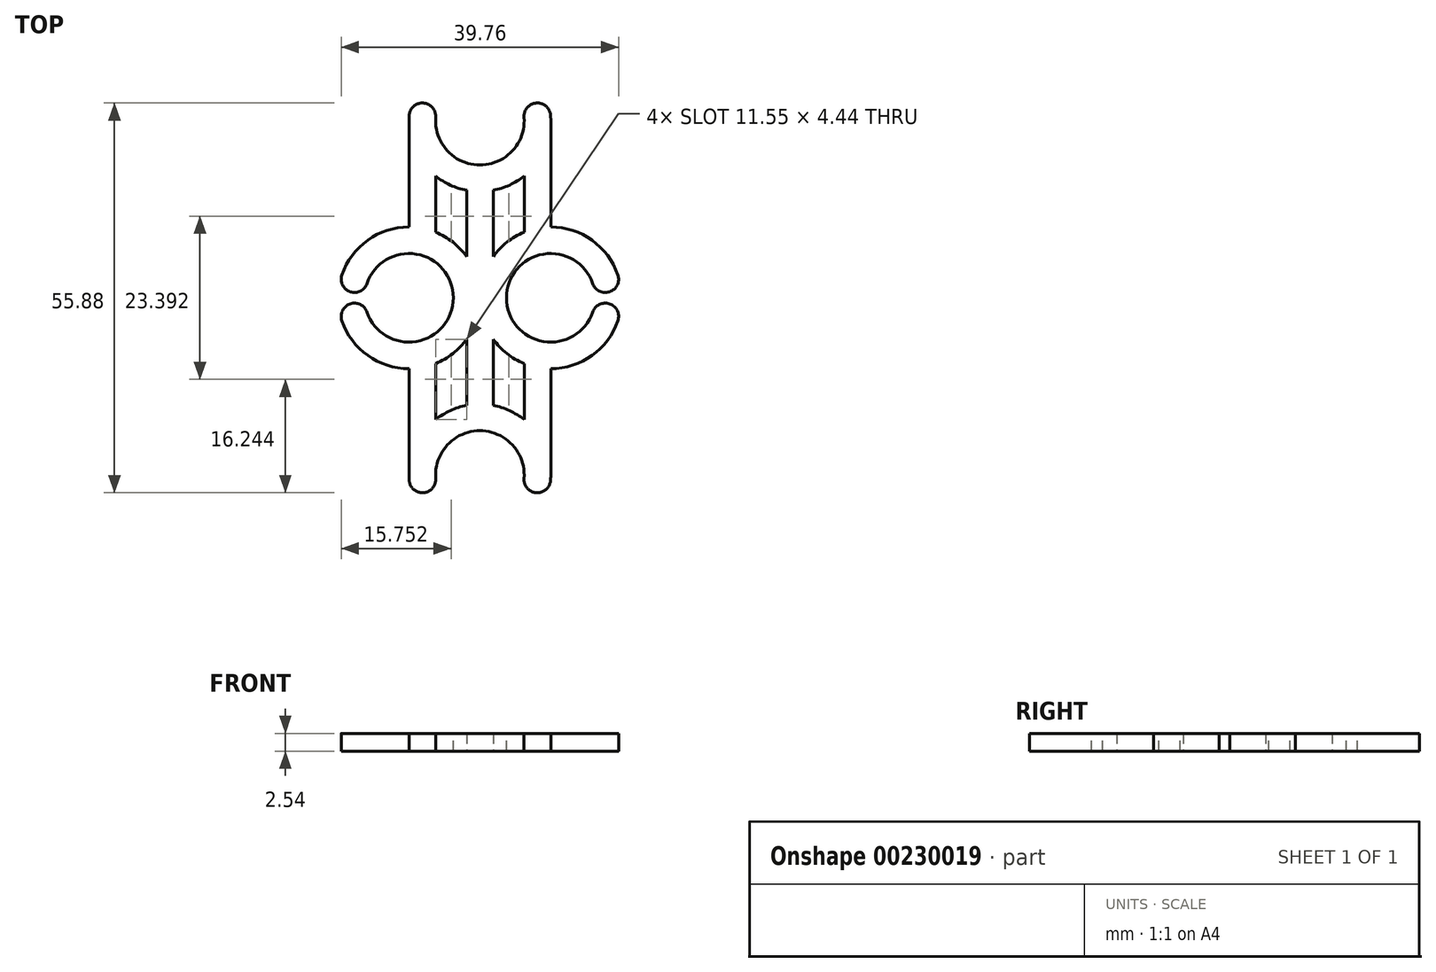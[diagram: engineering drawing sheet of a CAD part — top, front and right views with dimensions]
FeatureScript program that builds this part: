
annotation { "Feature Type Name" : "Feature", "Feature Type Description" : "" }
export const myFeature = defineFeature(function(context is Context, id is Id, definition is map)
    precondition{}
    {
        {
            var Q0;
            Q0=qCreatedBy(makeId("Top.planeOp"),FACE);
            var sketch = newSketch(context, id + "F0", { "sketchPlane" : qUnion([Q0])});
            skLineSegment(sketch, "E0", {"start": v(0, -25.4) * mm, "end": v(0, 25.4) * mm, "construction": true});
            skArc(sketch, "E1", {"start": v(-9.84, 27.94) * mm, "mid": v(0, 15.24) * mm, "end": v(9.84, 27.94) * mm});
            skArc(sketch, "E2", {"start": v(9.84, -27.94) * mm, "mid": v(0, -15.24) * mm, "end": v(-9.84, -27.94) * mm});
            skLineSegment(sketch, "E3.bottom", {"start": v(-1.9, 25.4) * mm, "end": v(1.9, 25.4) * mm});
            skLineSegment(sketch, "E3.top", {"start": v(-1.9, -25.4) * mm, "end": v(1.9, -25.4) * mm});
            skLineSegment(sketch, "E3.left", {"start": v(-1.9, 25.4) * mm, "end": v(-1.9, -25.4) * mm});
            skLineSegment(sketch, "E3.right", {"start": v(1.9, 25.4) * mm, "end": v(1.9, -25.4) * mm});
            skLineSegment(sketch, "E4", {"start": v(-9.84, 27.94) * mm, "end": v(9.84, 27.94) * mm});
            skLineSegment(sketch, "E5", {"start": v(-9.84, -27.94) * mm, "end": v(9.84, -27.94) * mm});
            skLineSegment(sketch, "E6", {"start": v(-10.16, 0) * mm, "end": v(10.16, 0) * mm, "construction": true});
            skPoint(sketch, "E7", {"position": v(0, 0) * mm});
            skCircle(sketch, "E8", {"center": v(-10.16, 0) * mm, "radius": 10.16 * mm});
            skCircle(sketch, "E9", {"center": v(10.16, 0) * mm, "radius": 10.16 * mm});
            skSolve(sketch);
        }
        {
            var Q0;
            Q0 = qSketchRegion(id + "F0", true);
            extrude(context, id + "F1", {"entities" : qUnion([Q0]), "depth" : 2.54 * mm});
        }
        {
            var Q0;
            Q0=makeQuery(id+"F1.opExtrude","CAP_FACE",FACE,{"disambiguationData":[OSD([sQuery(id+"F0.wireOp",EDGE,"Vd3e2Aaa-RSyU-HRI3-QYuA-ZNUXVVFevwxr"),sQuery(id+"F0.wireOp",EDGE,"BYLcNjdj-XaZf-7qvr-jPH4-58Jk393fSOor"),sQuery(id+"F0.wireOp",EDGE,"E1"),sQuery(id+"F0.wireOp",EDGE,"E2"),sQuery(id+"F0.wireOp",EDGE,"E3.left"),sQuery(id+"F0.wireOp",EDGE,"E3.right"),sQuery(id+"F0.wireOp",EDGE,"E4"),sQuery(id+"F0.wireOp",EDGE,"E5")])],"isStart":false});
            var sketch = newSketch(context, id + "F2", { "sketchPlane" : qUnion([Q0])});
            skCircle(sketch, "E10", {"center": v(0, 25.4) * mm, "radius": 6.35 * mm});
            skCircle(sketch, "E11", {"center": v(10.16, 0) * mm, "radius": 6.35 * mm});
            skCircle(sketch, "E12", {"center": v(-10.16, 0) * mm, "radius": 6.35 * mm});
            skCircle(sketch, "E13", {"center": v(0, -25.4) * mm, "radius": 6.35 * mm});
            skSolve(sketch);
        }
        {
            var Q0;
            Q0 = qSketchRegion(id + "F2", true);
            extrude(context, id + "F3", {"entities" : qUnion([Q0]), "operationType" : NewBodyOperationType.REMOVE, "oppositeDirection" : true, "depth" : 25.4 * mm});
        }
        {
            var Q0;
            Q0=makeQuery(id+"F1.opExtrude","CAP_FACE",FACE,{"disambiguationData":[OSD([sQuery(id+"F0.wireOp",EDGE,"E1"),sQuery(id+"F0.wireOp",EDGE,"E2"),sQuery(id+"F0.wireOp",EDGE,"E3.left"),sQuery(id+"F0.wireOp",EDGE,"E3.right"),sQuery(id+"F0.wireOp",EDGE,"E4"),sQuery(id+"F0.wireOp",EDGE,"E5"),sQuery(id+"F0.wireOp",EDGE,"E8"),sQuery(id+"F0.wireOp",EDGE,"E9")])],"isStart":false});
            var sketch = newSketch(context, id + "F4", { "sketchPlane" : qUnion([Q0])});
            skLineSegment(sketch, "E14", {"start": v(10.16, -25.4) * mm, "end": v(10.16, -10.16) * mm});
            skLineSegment(sketch, "E15", {"start": v(6.35, -17.47) * mm, "end": v(6.35, -9.42) * mm});
            skArc(sketch, "E16", {"start": v(10.16, -25.4) * mm, "mid": v(9.16, -21) * mm, "end": v(6.35, -17.47) * mm});
            skArc(sketch, "E17", {"start": v(6.35, -9.42) * mm, "mid": v(8.22, -9.97) * mm, "end": v(10.16, -10.16) * mm});
            skLineSegment(sketch, "E18.MirrorCS", {"start": v(-6.35, -17.47) * mm, "end": v(-6.35, -9.42) * mm});
            skLineSegment(sketch, "E19.MirrorCS", {"start": v(-10.16, -25.4) * mm, "end": v(-10.16, -10.16) * mm});
            skArc(sketch, "E20.MirrorCS", {"start": v(-6.35, -9.42) * mm, "mid": v(-8.22, -9.97) * mm, "end": v(-10.16, -10.16) * mm});
            skArc(sketch, "E21.MirrorCS", {"start": v(-10.16, -25.4) * mm, "mid": v(-9.16, -21) * mm, "end": v(-6.35, -17.47) * mm});
            skArc(sketch, "E22.MirrorCS", {"start": v(10.16, 25.4) * mm, "mid": v(9.16, 21) * mm, "end": v(6.35, 17.47) * mm});
            skLineSegment(sketch, "E23.MirrorCS", {"start": v(-10.16, 25.4) * mm, "end": v(-10.16, 10.16) * mm});
            skArc(sketch, "E24.MirrorCS", {"start": v(-10.16, 25.4) * mm, "mid": v(-9.16, 21) * mm, "end": v(-6.35, 17.47) * mm});
            skLineSegment(sketch, "E25.MirrorCS", {"start": v(10.16, 25.4) * mm, "end": v(10.16, 10.16) * mm});
            skLineSegment(sketch, "E26.MirrorCS", {"start": v(6.35, 17.47) * mm, "end": v(6.35, 9.42) * mm});
            skArc(sketch, "E27.MirrorCS", {"start": v(-6.35, 9.42) * mm, "mid": v(-8.22, 9.97) * mm, "end": v(-10.16, 10.16) * mm});
            skArc(sketch, "E28.MirrorCS", {"start": v(6.35, 9.42) * mm, "mid": v(8.22, 9.97) * mm, "end": v(10.16, 10.16) * mm});
            skLineSegment(sketch, "E29.MirrorCS", {"start": v(-6.35, 17.47) * mm, "end": v(-6.35, 9.42) * mm});
            skSolve(sketch);
        }
        {
            var Q0;
            Q0 = qSketchRegion(id + "F4", true);
            var Q1;
            Q1=makeQuery(id+"F1.opExtrude","CAP_FACE",FACE,{"disambiguationData":[OSD([sQuery(id+"F0.wireOp",EDGE,"E1"),sQuery(id+"F0.wireOp",EDGE,"E2"),sQuery(id+"F0.wireOp",EDGE,"E3.left"),sQuery(id+"F0.wireOp",EDGE,"E3.right"),sQuery(id+"F0.wireOp",EDGE,"E4"),sQuery(id+"F0.wireOp",EDGE,"E5"),sQuery(id+"F0.wireOp",EDGE,"E8"),sQuery(id+"F0.wireOp",EDGE,"E9")])],"isStart":true});
            extrude(context, id + "F5", {"entities" : qUnion([Q0]), "operationType" : NewBodyOperationType.ADD, "endBound" : BoundingType.UP_TO_SURFACE, "oppositeDirection" : true, "endBoundEntityFace" : qUnion([Q1]), "depth" : 25.4 * mm});
        }
        {
            var Q0;
            Q0=makeQuery(id+"F5.boolean.opBoolean","MERGE",FACE,{"derivedFrom":[makeQuery(id+"F1.opExtrude","CAP_FACE",FACE,{"disambiguationData":[OSD([sQuery(id+"F0.wireOp",EDGE,"E1"),sQuery(id+"F0.wireOp",EDGE,"E2"),sQuery(id+"F0.wireOp",EDGE,"E3.left"),sQuery(id+"F0.wireOp",EDGE,"E3.right"),sQuery(id+"F0.wireOp",EDGE,"E4"),sQuery(id+"F0.wireOp",EDGE,"E5"),sQuery(id+"F0.wireOp",EDGE,"E8"),sQuery(id+"F0.wireOp",EDGE,"E9")])],"isStart":false}),makeQuery(id+"F5.opExtrude","CAP_FACE",FACE,{"disambiguationData":[OSD([sQuery(id+"F4.wireOp",EDGE,"E14"),sQuery(id+"F4.wireOp",EDGE,"E15"),sQuery(id+"F4.wireOp",EDGE,"E16"),sQuery(id+"F4.wireOp",EDGE,"E17")])],"isStart":true}),makeQuery(id+"F5.opExtrude","CAP_FACE",FACE,{"disambiguationData":[OSD([sQuery(id+"F4.wireOp",EDGE,"E18.MirrorCS"),sQuery(id+"F4.wireOp",EDGE,"E19.MirrorCS"),sQuery(id+"F4.wireOp",EDGE,"E20.MirrorCS"),sQuery(id+"F4.wireOp",EDGE,"E21.MirrorCS")])],"isStart":true}),makeQuery(id+"F5.opExtrude","CAP_FACE",FACE,{"disambiguationData":[OSD([sQuery(id+"F4.wireOp",EDGE,"E22.MirrorCS"),sQuery(id+"F4.wireOp",EDGE,"E25.MirrorCS"),sQuery(id+"F4.wireOp",EDGE,"E26.MirrorCS"),sQuery(id+"F4.wireOp",EDGE,"E28.MirrorCS")])],"isStart":true}),makeQuery(id+"F5.opExtrude","CAP_FACE",FACE,{"disambiguationData":[OSD([sQuery(id+"F4.wireOp",EDGE,"E23.MirrorCS"),sQuery(id+"F4.wireOp",EDGE,"E24.MirrorCS"),sQuery(id+"F4.wireOp",EDGE,"E27.MirrorCS"),sQuery(id+"F4.wireOp",EDGE,"E29.MirrorCS")])],"isStart":true})]});
            var sketch = newSketch(context, id + "F6", { "sketchPlane" : qUnion([Q0])});
            skLineSegment(sketch, "E30.bottom", {"start": v(10.16, -0.76) * mm, "end": v(29.15, -0.76) * mm});
            skLineSegment(sketch, "E30.top", {"start": v(10.16, 0.76) * mm, "end": v(29.15, 0.76) * mm});
            skLineSegment(sketch, "E30.left", {"start": v(10.16, -0.76) * mm, "end": v(10.16, 0.76) * mm});
            skLineSegment(sketch, "E30.right", {"start": v(29.15, -0.76) * mm, "end": v(29.15, 0.76) * mm});
            skLineSegment(sketch, "E31.MirrorCS", {"start": v(-10.16, -0.76) * mm, "end": v(-10.16, 0.76) * mm});
            skLineSegment(sketch, "E32.MirrorCS", {"start": v(-29.15, -0.76) * mm, "end": v(-29.15, 0.76) * mm});
            skLineSegment(sketch, "E33.MirrorCS", {"start": v(-10.16, -0.76) * mm, "end": v(-29.15, -0.76) * mm});
            skLineSegment(sketch, "E34.MirrorCS", {"start": v(-10.16, 0.76) * mm, "end": v(-29.15, 0.76) * mm});
            skSolve(sketch);
        }
        {
            var Q0;
            Q0 = qSketchRegion(id + "F6", true);
            extrude(context, id + "F7", {"entities" : qUnion([Q0]), "operationType" : NewBodyOperationType.REMOVE, "oppositeDirection" : true, "depth" : 25.4 * mm});
        }
        {
            var Q0;
            {var subQ12=sQuery(id+"F0.wireOp",EDGE,"E9");var subQ23=sQuery(id+"F4.wireOp",EDGE,"E14");Q0=makeQuery(id+"F7.boolean.opBoolean","INTERSECT",EDGE,{"derivedFrom":[makeQuery(id+"F5.boolean.opBoolean","SPLIT",FACE,{"disambiguationData":[TD([makeQuery(id+"F5.opExtrude","SWEPT_FACE",FACE,{"disambiguationData":[OSD([subQ23])]})])],"derivedFrom":makeQuery(id+"F1.opExtrude","SWEPT_FACE",FACE,{"disambiguationData":[OSD([subQ12])]})}),makeQuery(id+"F7.opExtrude","SWEPT_FACE",FACE,{"disambiguationData":[OSD([sQuery(id+"F6.wireOp",EDGE,"E30.bottom")])]})]});}
            var Q1;
            {var subQ12=sQuery(id+"F0.wireOp",EDGE,"E9");var subQ23=sQuery(id+"F4.wireOp",EDGE,"E14");Q1=makeQuery(id+"F7.boolean.opBoolean","INTERSECT",EDGE,{"derivedFrom":[makeQuery(id+"F5.boolean.opBoolean","SPLIT",FACE,{"disambiguationData":[TD([makeQuery(id+"F5.opExtrude","SWEPT_FACE",FACE,{"disambiguationData":[OSD([subQ23])]})])],"derivedFrom":makeQuery(id+"F1.opExtrude","SWEPT_FACE",FACE,{"disambiguationData":[OSD([subQ12])]})}),makeQuery(id+"F7.opExtrude","SWEPT_FACE",FACE,{"disambiguationData":[OSD([sQuery(id+"F6.wireOp",EDGE,"E30.top")])]})]});}
            var Q2;
            Q2=makeQuery(id+"F7.boolean.opBoolean","INTERSECT",EDGE,{"derivedFrom":[makeQuery(id+"F3.boolean.opBoolean","COPY",FACE,{"derivedFrom":makeQuery(id+"F3.opExtrude","SWEPT_FACE",FACE,{"disambiguationData":[OSD([sQuery(id+"F2.wireOp",EDGE,"E11")])]})}),makeQuery(id+"F7.opExtrude","SWEPT_FACE",FACE,{"disambiguationData":[OSD([sQuery(id+"F6.wireOp",EDGE,"E30.bottom")])]})]});
            var Q3;
            Q3=makeQuery(id+"F7.boolean.opBoolean","INTERSECT",EDGE,{"derivedFrom":[makeQuery(id+"F3.boolean.opBoolean","COPY",FACE,{"derivedFrom":makeQuery(id+"F3.opExtrude","SWEPT_FACE",FACE,{"disambiguationData":[OSD([sQuery(id+"F2.wireOp",EDGE,"E11")])]})}),makeQuery(id+"F7.opExtrude","SWEPT_FACE",FACE,{"disambiguationData":[OSD([sQuery(id+"F6.wireOp",EDGE,"E30.top")])]})]});
            var Q4;
            Q4=makeQuery(id+"F3.boolean.opBoolean","INTERSECT",EDGE,{"disambiguationData":[OD(0.0)],"derivedFrom":[makeQuery(id+"F1.opExtrude","SWEPT_FACE",FACE,{"disambiguationData":[OSD([sQuery(id+"F0.wireOp",EDGE,"E5")])]}),makeQuery(id+"F3.opExtrude","SWEPT_FACE",FACE,{"disambiguationData":[OSD([sQuery(id+"F2.wireOp",EDGE,"E13")])]})]});
            var Q5;
            {var subQ0=sQuery(id+"F0.wireOp",EDGE,"E5");var subQ1=sQuery(id+"F0.wireOp",EDGE,"E2");Q5=makeQuery(id+"F1.opExtrude","SWEPT_EDGE",EDGE,{"disambiguationData":[OSD([subQ1,subQ0]),TDD([makeQuery(id+"F0.imprint","INTERSECT",VERTEX,{"disambiguationData":[OD(0.0)],"derivedFrom":[subQ1,subQ0]})])]});}
            var Q6;
            Q6=makeQuery(id+"F3.boolean.opBoolean","INTERSECT",EDGE,{"disambiguationData":[OD(1.0)],"derivedFrom":[makeQuery(id+"F1.opExtrude","SWEPT_FACE",FACE,{"disambiguationData":[OSD([sQuery(id+"F0.wireOp",EDGE,"E5")])]}),makeQuery(id+"F3.opExtrude","SWEPT_FACE",FACE,{"disambiguationData":[OSD([sQuery(id+"F2.wireOp",EDGE,"E13")])]})]});
            var Q7;
            {var subQ0=sQuery(id+"F0.wireOp",EDGE,"E5");var subQ1=sQuery(id+"F0.wireOp",EDGE,"E2");Q7=makeQuery(id+"F1.opExtrude","SWEPT_EDGE",EDGE,{"disambiguationData":[OSD([subQ1,subQ0]),TDD([makeQuery(id+"F0.imprint","INTERSECT",VERTEX,{"disambiguationData":[OD(1.0)],"derivedFrom":[subQ1,subQ0]})])]});}
            var Q8;
            {var subQ5=sQuery(id+"F4.wireOp",EDGE,"E19.MirrorCS");var subQ10=sQuery(id+"F0.wireOp",EDGE,"E8");Q8=makeQuery(id+"F7.boolean.opBoolean","INTERSECT",EDGE,{"derivedFrom":[makeQuery(id+"F5.boolean.opBoolean","SPLIT",FACE,{"disambiguationData":[TD([makeQuery(id+"F5.opExtrude","SWEPT_FACE",FACE,{"disambiguationData":[OSD([subQ5])]})])],"derivedFrom":makeQuery(id+"F1.opExtrude","SWEPT_FACE",FACE,{"disambiguationData":[OSD([subQ10])]})}),makeQuery(id+"F7.opExtrude","SWEPT_FACE",FACE,{"disambiguationData":[OSD([sQuery(id+"F6.wireOp",EDGE,"E34.MirrorCS")])]})]});}
            var Q9;
            {var subQ5=sQuery(id+"F4.wireOp",EDGE,"E19.MirrorCS");var subQ10=sQuery(id+"F0.wireOp",EDGE,"E8");Q9=makeQuery(id+"F7.boolean.opBoolean","INTERSECT",EDGE,{"derivedFrom":[makeQuery(id+"F5.boolean.opBoolean","SPLIT",FACE,{"disambiguationData":[TD([makeQuery(id+"F5.opExtrude","SWEPT_FACE",FACE,{"disambiguationData":[OSD([subQ5])]})])],"derivedFrom":makeQuery(id+"F1.opExtrude","SWEPT_FACE",FACE,{"disambiguationData":[OSD([subQ10])]})}),makeQuery(id+"F7.opExtrude","SWEPT_FACE",FACE,{"disambiguationData":[OSD([sQuery(id+"F6.wireOp",EDGE,"E33.MirrorCS")])]})]});}
            var Q10;
            Q10=makeQuery(id+"F7.boolean.opBoolean","INTERSECT",EDGE,{"derivedFrom":[makeQuery(id+"F3.boolean.opBoolean","COPY",FACE,{"derivedFrom":makeQuery(id+"F3.opExtrude","SWEPT_FACE",FACE,{"disambiguationData":[OSD([sQuery(id+"F2.wireOp",EDGE,"E12")])]})}),makeQuery(id+"F7.opExtrude","SWEPT_FACE",FACE,{"disambiguationData":[OSD([sQuery(id+"F6.wireOp",EDGE,"E33.MirrorCS")])]})]});
            var Q11;
            Q11=makeQuery(id+"F7.boolean.opBoolean","INTERSECT",EDGE,{"derivedFrom":[makeQuery(id+"F3.boolean.opBoolean","COPY",FACE,{"derivedFrom":makeQuery(id+"F3.opExtrude","SWEPT_FACE",FACE,{"disambiguationData":[OSD([sQuery(id+"F2.wireOp",EDGE,"E12")])]})}),makeQuery(id+"F7.opExtrude","SWEPT_FACE",FACE,{"disambiguationData":[OSD([sQuery(id+"F6.wireOp",EDGE,"E34.MirrorCS")])]})]});
            var Q12;
            {var subQ0=sQuery(id+"F0.wireOp",EDGE,"E4");var subQ1=sQuery(id+"F0.wireOp",EDGE,"E1");Q12=makeQuery(id+"F1.opExtrude","SWEPT_EDGE",EDGE,{"disambiguationData":[OSD([subQ1,subQ0]),TDD([makeQuery(id+"F0.imprint","INTERSECT",VERTEX,{"disambiguationData":[OD(0.0)],"derivedFrom":[subQ1,subQ0]})])]});}
            var Q13;
            Q13=makeQuery(id+"F3.boolean.opBoolean","INTERSECT",EDGE,{"disambiguationData":[OD(0.0)],"derivedFrom":[makeQuery(id+"F1.opExtrude","SWEPT_FACE",FACE,{"disambiguationData":[OSD([sQuery(id+"F0.wireOp",EDGE,"E4")])]}),makeQuery(id+"F3.opExtrude","SWEPT_FACE",FACE,{"disambiguationData":[OSD([sQuery(id+"F2.wireOp",EDGE,"E10")])]})]});
            var Q14;
            Q14=makeQuery(id+"F3.boolean.opBoolean","INTERSECT",EDGE,{"disambiguationData":[OD(1.0)],"derivedFrom":[makeQuery(id+"F1.opExtrude","SWEPT_FACE",FACE,{"disambiguationData":[OSD([sQuery(id+"F0.wireOp",EDGE,"E4")])]}),makeQuery(id+"F3.opExtrude","SWEPT_FACE",FACE,{"disambiguationData":[OSD([sQuery(id+"F2.wireOp",EDGE,"E10")])]})]});
            var Q15;
            {var subQ0=sQuery(id+"F0.wireOp",EDGE,"E4");var subQ1=sQuery(id+"F0.wireOp",EDGE,"E1");Q15=makeQuery(id+"F1.opExtrude","SWEPT_EDGE",EDGE,{"disambiguationData":[OSD([subQ1,subQ0]),TDD([makeQuery(id+"F0.imprint","INTERSECT",VERTEX,{"disambiguationData":[OD(1.0)],"derivedFrom":[subQ1,subQ0]})])]});}
            fillet(context, id + "F8", {"entities" : qUnion([Q0, Q1, Q2, Q3, Q4, Q5, Q6, Q7, Q8, Q9, Q10, Q11, Q12, Q13, Q14, Q15]), "radius" : 1.9 * mm, "tangentPropagation" : true, "allowEdgeOverflow" : false});
        }
    });
